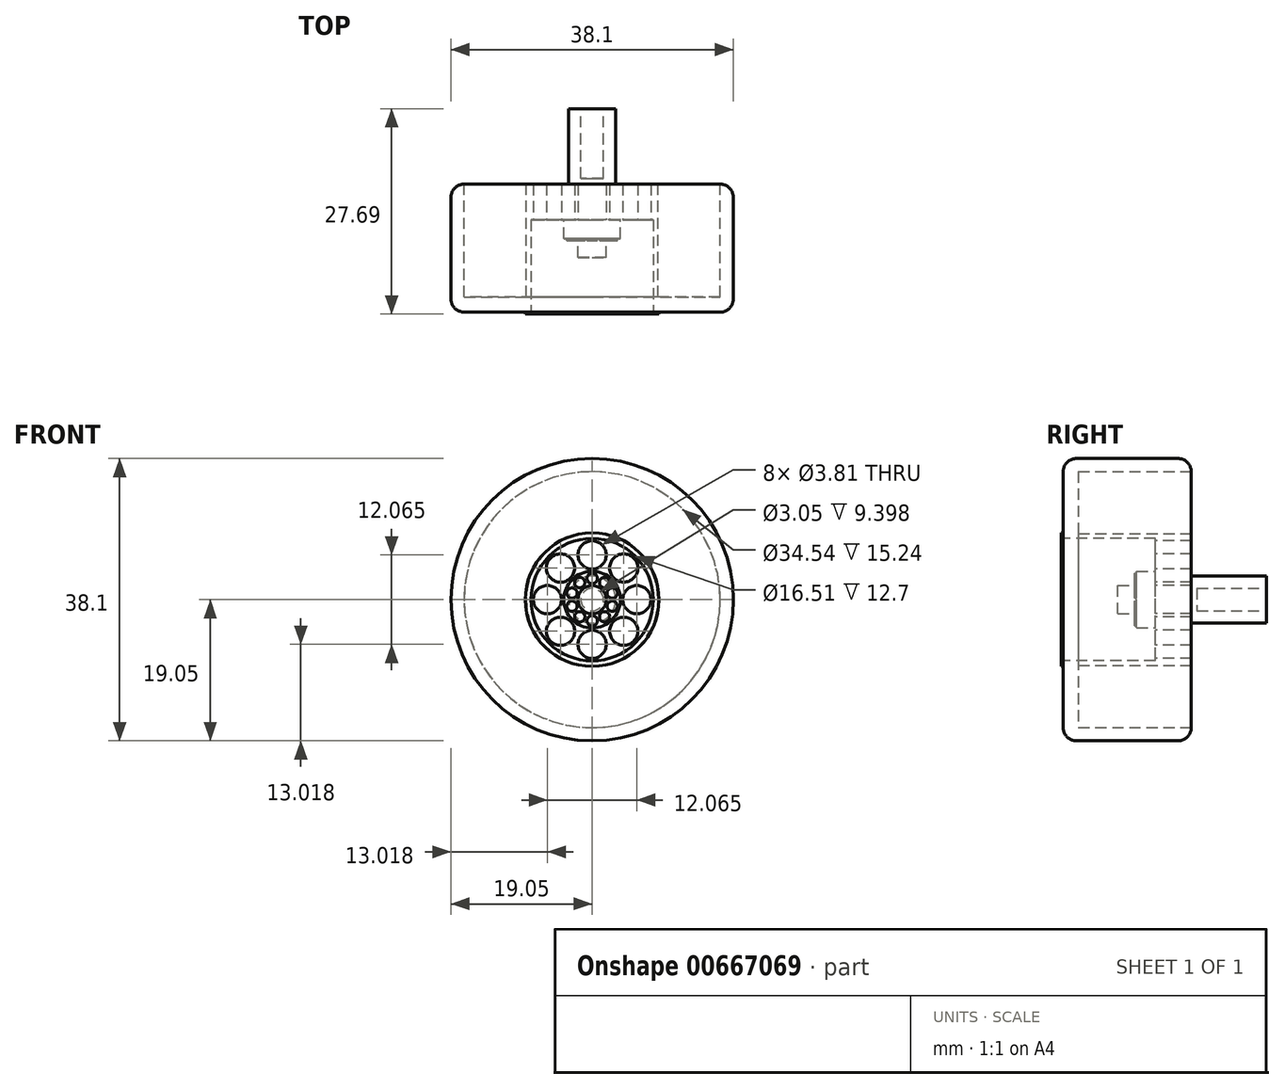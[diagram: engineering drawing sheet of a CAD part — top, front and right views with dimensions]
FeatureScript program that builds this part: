
annotation { "Feature Type Name" : "Feature", "Feature Type Description" : "" }
export const myFeature = defineFeature(function(context is Context, id is Id, definition is map)
    precondition{}
    {
        {
            var Q0;
            Q0=qCreatedBy(makeId("Front.planeOp"),FACE);
            var sketch = newSketch(context, id + "F0", { "sketchPlane" : qUnion([Q0])});
            skCircle(sketch, "E0", {"center": v(0, 0) * mm, "radius": 19.05 * mm});
            skSolve(sketch);
        }
        {
            var Q0;
            Q0=makeQuery(id+"F0.imprint","IMPRINT",FACE,{"disambiguationData":[TD([[makeQuery(id+"F0.imprint","IMPRINT",EDGE,{"derivedFrom":sQuery(id+"F0.wireOp",EDGE,"E0")}),1.0]])]});
            extrude(context, id + "F1", {"entities" : qUnion([Q0]), "depth" : 17.27 * mm, "offsetDistance" : 25.4 * mm});
        }
        {
            var Q0;
            Q0=makeQuery(id+"F1.opExtrude","CAP_FACE",FACE,{"disambiguationData":[OSD([sQuery(id+"F0.wireOp",EDGE,"E0")])],"isStart":true});
            var sketch = newSketch(context, id + "F2", { "sketchPlane" : qUnion([Q0])});
            skCircle(sketch, "E1", {"center": v(0, 0) * mm, "radius": 3.18 * mm});
            skSolve(sketch);
        }
        {
            var Q0;
            Q0=makeQuery(id+"F2.imprint","IMPRINT",FACE,{"disambiguationData":[TD([[makeQuery(id+"F2.imprint","IMPRINT",EDGE,{"derivedFrom":sQuery(id+"F2.wireOp",EDGE,"E1")}),1.0]])]});
            extrude(context, id + "F3", {"entities" : qUnion([Q0]), "operationType" : NewBodyOperationType.ADD, "depth" : 10.16 * mm, "offsetDistance" : 25.4 * mm});
        }
        {
            var Q0;
            Q0=makeQuery(id+"F3.opExtrude","CAP_FACE",FACE,{"disambiguationData":[OSD([sQuery(id+"F2.wireOp",EDGE,"E1")])],"isStart":false});
            var sketch = newSketch(context, id + "F4", { "sketchPlane" : qUnion([Q0])});
            skCircle(sketch, "E2", {"center": v(0, 0) * mm, "radius": 1.52 * mm});
            skSolve(sketch);
        }
        {
            var Q0;
            Q0=makeQuery(id+"F4.imprint","IMPRINT",FACE,{"disambiguationData":[TD([[makeQuery(id+"F4.imprint","IMPRINT",EDGE,{"derivedFrom":sQuery(id+"F4.wireOp",EDGE,"E2")}),1.0]])]});
            extrude(context, id + "F5", {"entities" : qUnion([Q0]), "operationType" : NewBodyOperationType.REMOVE, "oppositeDirection" : true, "depth" : 9.4 * mm, "offsetDistance" : 25.4 * mm});
        }
        {
            var Q0;
            Q0=makeQuery(id+"F1.opExtrude","CAP_FACE",FACE,{"disambiguationData":[OSD([sQuery(id+"F0.wireOp",EDGE,"E0")])],"isStart":true});
            var sketch = newSketch(context, id + "F6", { "sketchPlane" : qUnion([Q0])});
            skCircle(sketch, "E3", {"center": v(0, 0) * mm, "radius": 17.27 * mm});
            skSolve(sketch);
        }
        {
            var Q0;
            Q0=makeQuery(id+"F1.opExtrude","CAP_FACE",FACE,{"disambiguationData":[OSD([sQuery(id+"F0.wireOp",EDGE,"E0")])],"isStart":false});
            var sketch = newSketch(context, id + "F7", { "sketchPlane" : qUnion([Q0])});
            skCircle(sketch, "E4", {"center": v(0, 0) * mm, "radius": 8.9 * mm});
            skCircle(sketch, "E5", {"center": v(0, 0) * mm, "radius": 8.26 * mm});
            skSolve(sketch);
        }
        {
            var Q0;
            Q0=makeQuery(id+"F7.imprint","IMPRINT",FACE,{"disambiguationData":[TD([[makeQuery(id+"F7.imprint","IMPRINT",EDGE,{"derivedFrom":sQuery(id+"F7.wireOp",EDGE,"E5")}),1.0]])]});
            extrude(context, id + "F8", {"entities" : qUnion([Q0]), "operationType" : NewBodyOperationType.REMOVE, "oppositeDirection" : true, "depth" : 12.45 * mm, "offsetDistance" : 25.4 * mm});
        }
        {
            var Q0;
            Q0=makeQuery(id+"F6.imprint","IMPRINT",FACE,{"disambiguationData":[TD([[makeQuery(id+"F6.imprint","IMPRINT",EDGE,{"derivedFrom":sQuery(id+"F6.wireOp",EDGE,"E3")}),1.0]])]});
            var sketch = newSketch(context, id + "F9", { "sketchPlane" : qUnion([Q0])});
            skCircle(sketch, "E6", {"center": v(0, 0) * mm, "radius": 8.9 * mm});
            skSolve(sketch);
        }
        {
            var Q0;
            Q0=makeQuery(id+"F9.imprint","IMPRINT",FACE,{"disambiguationData":[TD([[makeQuery(id+"F9.imprint","IMPRINT",EDGE,{"derivedFrom":sQuery(id+"F9.wireOp",EDGE,"E6")}),-1.0]])]});
            extrude(context, id + "F10", {"entities" : qUnion([Q0]), "operationType" : NewBodyOperationType.REMOVE, "oppositeDirection" : true, "depth" : 15.24 * mm, "offsetDistance" : 25.4 * mm});
        }
        {
            var Q0;
            Q0=makeQuery(id+"F1.opExtrude","CAP_FACE",FACE,{"disambiguationData":[OSD([sQuery(id+"F0.wireOp",EDGE,"E0")])],"isStart":false});
            var sketch = newSketch(context, id + "F11", { "sketchPlane" : qUnion([Q0])});
            skCircle(sketch, "E7", {"center": v(0, 0) * mm, "radius": 9.02 * mm});
            skSolve(sketch);
        }
        {
            var Q0;
            Q0=makeQuery(id+"F11.imprint","IMPRINT",FACE,{"disambiguationData":[TD([[makeQuery(id+"F11.imprint","IMPRINT",EDGE,{"derivedFrom":sQuery(id+"F11.wireOp",EDGE,"E7")}),1.0]])]});
            extrude(context, id + "F12", {"entities" : qUnion([Q0]), "operationType" : NewBodyOperationType.ADD, "depth" : 0.25 * mm, "offsetDistance" : 25.4 * mm});
        }
        {
            var Q0;
            Q0=makeQuery(id+"F8.boolean.opBoolean","COPY",FACE,{"derivedFrom":makeQuery(id+"F8.opExtrude","CAP_FACE",FACE,{"disambiguationData":[OSD([sQuery(id+"F7.wireOp",EDGE,"E5")])],"isStart":false})});
            var sketch = newSketch(context, id + "F13", { "sketchPlane" : qUnion([Q0])});
            skCircle(sketch, "E8", {"center": v(0, 0) * mm, "radius": 1.9 * mm});
            skSolve(sketch);
        }
        {
            var Q0;
            Q0=makeQuery(id+"F13.imprint","IMPRINT",FACE,{"disambiguationData":[TD([[makeQuery(id+"F13.imprint","IMPRINT",EDGE,{"derivedFrom":sQuery(id+"F13.wireOp",EDGE,"E8")}),1.0]])]});
            extrude(context, id + "F14", {"entities" : qUnion([Q0]), "operationType" : NewBodyOperationType.ADD, "depth" : 5.08 * mm, "offsetDistance" : 25.4 * mm});
        }
        {
            var Q0;
            Q0=makeQuery(id+"F8.boolean.opBoolean","COPY",FACE,{"derivedFrom":makeQuery(id+"F8.opExtrude","CAP_FACE",FACE,{"disambiguationData":[OSD([sQuery(id+"F7.wireOp",EDGE,"E5")])],"isStart":false})});
            var sketch = newSketch(context, id + "F15", { "sketchPlane" : qUnion([Q0])});
            skCircle(sketch, "E9", {"center": v(0, 0) * mm, "radius": 3.81 * mm});
            skSolve(sketch);
        }
        {
            var Q0;
            Q0=makeQuery(id+"F15.imprint","IMPRINT",FACE,{"disambiguationData":[TD([[makeQuery(id+"F15.imprint","IMPRINT",EDGE,{"derivedFrom":sQuery(id+"F15.wireOp",EDGE,"E9")}),1.0]])]});
            extrude(context, id + "F16", {"entities" : qUnion([Q0]), "operationType" : NewBodyOperationType.ADD, "depth" : 2.54 * mm, "offsetDistance" : 25.4 * mm});
        }
        {
            var Q0;
            Q0=makeQuery(id+"F8.boolean.opBoolean","COPY",FACE,{"derivedFrom":makeQuery(id+"F8.opExtrude","CAP_FACE",FACE,{"disambiguationData":[OSD([sQuery(id+"F7.wireOp",EDGE,"E5")])],"isStart":false})});
            var sketch = newSketch(context, id + "F17", { "sketchPlane" : qUnion([Q0])});
            skCircle(sketch, "E10", {"center": v(0, 6.03) * mm, "radius": 1.9 * mm});
            skCircle(sketch, "E11", {"center": v(0, -6.03) * mm, "radius": 1.9 * mm});
            skCircle(sketch, "E12", {"center": v(4.27, -4.26) * mm, "radius": 1.9 * mm});
            skCircle(sketch, "E13", {"center": v(6.03, 0) * mm, "radius": 1.9 * mm});
            skCircle(sketch, "E14", {"center": v(4.26, 4.27) * mm, "radius": 1.9 * mm});
            skCircle(sketch, "E15", {"center": v(-4.27, 4.26) * mm, "radius": 1.9 * mm});
            skCircle(sketch, "E16", {"center": v(-6.03, 0) * mm, "radius": 1.9 * mm});
            skCircle(sketch, "E17", {"center": v(-4.26, -4.27) * mm, "radius": 1.9 * mm});
            skSolve(sketch);
        }
        {
            var Q0;
            Q0=makeQuery(id+"F17.imprint","IMPRINT",FACE,{"disambiguationData":[TD([[makeQuery(id+"F17.imprint","IMPRINT",EDGE,{"derivedFrom":sQuery(id+"F17.wireOp",EDGE,"E15")}),1.0]])]});
            var Q1;
            Q1=makeQuery(id+"F17.imprint","IMPRINT",FACE,{"disambiguationData":[TD([[makeQuery(id+"F17.imprint","IMPRINT",EDGE,{"derivedFrom":sQuery(id+"F17.wireOp",EDGE,"E10")}),1.0]])]});
            var Q2;
            Q2=makeQuery(id+"F17.imprint","IMPRINT",FACE,{"disambiguationData":[TD([[makeQuery(id+"F17.imprint","IMPRINT",EDGE,{"derivedFrom":sQuery(id+"F17.wireOp",EDGE,"E14")}),1.0]])]});
            var Q3;
            Q3=makeQuery(id+"F17.imprint","IMPRINT",FACE,{"disambiguationData":[TD([[makeQuery(id+"F17.imprint","IMPRINT",EDGE,{"derivedFrom":sQuery(id+"F17.wireOp",EDGE,"E13")}),1.0]])]});
            var Q4;
            Q4=makeQuery(id+"F17.imprint","IMPRINT",FACE,{"disambiguationData":[TD([[makeQuery(id+"F17.imprint","IMPRINT",EDGE,{"derivedFrom":sQuery(id+"F17.wireOp",EDGE,"E12")}),1.0]])]});
            var Q5;
            Q5=makeQuery(id+"F17.imprint","IMPRINT",FACE,{"disambiguationData":[TD([[makeQuery(id+"F17.imprint","IMPRINT",EDGE,{"derivedFrom":sQuery(id+"F17.wireOp",EDGE,"E11")}),1.0]])]});
            var Q6;
            Q6=makeQuery(id+"F17.imprint","IMPRINT",FACE,{"disambiguationData":[TD([[makeQuery(id+"F17.imprint","IMPRINT",EDGE,{"derivedFrom":sQuery(id+"F17.wireOp",EDGE,"E17")}),1.0]])]});
            var Q7;
            Q7=makeQuery(id+"F17.imprint","IMPRINT",FACE,{"disambiguationData":[TD([[makeQuery(id+"F17.imprint","IMPRINT",EDGE,{"derivedFrom":sQuery(id+"F17.wireOp",EDGE,"E16")}),1.0]])]});
            extrude(context, id + "F18", {"entities" : qUnion([Q0, Q1, Q2, Q3, Q4, Q5, Q6, Q7]), "operationType" : NewBodyOperationType.REMOVE, "endBound" : BoundingType.THROUGH_ALL, "oppositeDirection" : true, "depth" : 25.4 * mm, "offsetDistance" : 25.4 * mm});
        }
        {
            var Q0;
            Q0=makeQuery(id+"F16.opExtrude","CAP_FACE",FACE,{"disambiguationData":[OSD([sQuery(id+"F13.wireOp",EDGE,"E8"),sQuery(id+"F15.wireOp",EDGE,"E9")])],"isStart":false});
            var sketch = newSketch(context, id + "F19", { "sketchPlane" : qUnion([Q0])});
            skCircle(sketch, "E18", {"center": v(0, 2.86) * mm, "radius": 0.7 * mm});
            skCircle(sketch, "E19.1.0", {"center": v(-1.68, 2.31) * mm, "radius": 0.7 * mm});
            skCircle(sketch, "E19.2.0", {"center": v(-2.72, 0.88) * mm, "radius": 0.7 * mm});
            skCircle(sketch, "E19.3.0", {"center": v(-2.72, -0.88) * mm, "radius": 0.7 * mm});
            skCircle(sketch, "E19.4.0", {"center": v(-1.68, -2.31) * mm, "radius": 0.7 * mm});
            skCircle(sketch, "E19.5.0", {"center": v(0, -2.86) * mm, "radius": 0.7 * mm});
            skCircle(sketch, "E19.6.0", {"center": v(1.68, -2.31) * mm, "radius": 0.7 * mm});
            skCircle(sketch, "E19.7.0", {"center": v(2.72, -0.88) * mm, "radius": 0.7 * mm});
            skCircle(sketch, "E19.8.0", {"center": v(2.72, 0.88) * mm, "radius": 0.7 * mm});
            skCircle(sketch, "E19.9.0", {"center": v(1.68, 2.31) * mm, "radius": 0.7 * mm});
            skPoint(sketch, "E19.center", {"position": v(0, 0) * mm});
            skSolve(sketch);
        }
        {
            var Q0;
            Q0=makeQuery(id+"F19.imprint","IMPRINT",FACE,{"disambiguationData":[TD([[makeQuery(id+"F19.imprint","IMPRINT",EDGE,{"derivedFrom":sQuery(id+"F19.wireOp",EDGE,"E19.1.0")}),1.0]])]});
            var Q1;
            Q1=makeQuery(id+"F19.imprint","IMPRINT",FACE,{"disambiguationData":[TD([[makeQuery(id+"F19.imprint","IMPRINT",EDGE,{"derivedFrom":sQuery(id+"F19.wireOp",EDGE,"E18")}),1.0]])]});
            var Q2;
            Q2=makeQuery(id+"F19.imprint","IMPRINT",FACE,{"disambiguationData":[TD([[makeQuery(id+"F19.imprint","IMPRINT",EDGE,{"derivedFrom":sQuery(id+"F19.wireOp",EDGE,"E19.9.0")}),1.0]])]});
            var Q3;
            Q3=makeQuery(id+"F19.imprint","IMPRINT",FACE,{"disambiguationData":[TD([[makeQuery(id+"F19.imprint","IMPRINT",EDGE,{"derivedFrom":sQuery(id+"F19.wireOp",EDGE,"E19.8.0")}),1.0]])]});
            var Q4;
            Q4=makeQuery(id+"F19.imprint","IMPRINT",FACE,{"disambiguationData":[TD([[makeQuery(id+"F19.imprint","IMPRINT",EDGE,{"derivedFrom":sQuery(id+"F19.wireOp",EDGE,"E19.6.0")}),1.0]])]});
            var Q5;
            Q5=makeQuery(id+"F19.imprint","IMPRINT",FACE,{"disambiguationData":[TD([[makeQuery(id+"F19.imprint","IMPRINT",EDGE,{"derivedFrom":sQuery(id+"F19.wireOp",EDGE,"E19.5.0")}),1.0]])]});
            var Q6;
            Q6=makeQuery(id+"F19.imprint","IMPRINT",FACE,{"disambiguationData":[TD([[makeQuery(id+"F19.imprint","IMPRINT",EDGE,{"derivedFrom":sQuery(id+"F19.wireOp",EDGE,"E19.7.0")}),1.0]])]});
            var Q7;
            Q7=makeQuery(id+"F19.imprint","IMPRINT",FACE,{"disambiguationData":[TD([[makeQuery(id+"F19.imprint","IMPRINT",EDGE,{"derivedFrom":sQuery(id+"F19.wireOp",EDGE,"E19.4.0")}),1.0]])]});
            var Q8;
            Q8=makeQuery(id+"F19.imprint","IMPRINT",FACE,{"disambiguationData":[TD([[makeQuery(id+"F19.imprint","IMPRINT",EDGE,{"derivedFrom":sQuery(id+"F19.wireOp",EDGE,"E19.3.0")}),1.0]])]});
            var Q9;
            Q9=makeQuery(id+"F19.imprint","IMPRINT",FACE,{"disambiguationData":[TD([[makeQuery(id+"F19.imprint","IMPRINT",EDGE,{"derivedFrom":sQuery(id+"F19.wireOp",EDGE,"E19.2.0")}),1.0]])]});
            extrude(context, id + "F20", {"entities" : qUnion([Q0, Q1, Q2, Q3, Q4, Q5, Q6, Q7, Q8, Q9]), "operationType" : NewBodyOperationType.ADD, "depth" : 0.25 * mm, "offsetDistance" : 25.4 * mm});
        }
        {
            var Q0;
            Q0=makeQuery(id+"F1.opExtrude","CAP_EDGE",EDGE,{"disambiguationData":[OSD([sQuery(id+"F0.wireOp",EDGE,"E0")])],"isStart":false});
            fillet(context, id + "F21", {"entities" : qUnion([Q0]), "radius" : 1.78 * mm, "tangentPropagation" : true, "allowEdgeOverflow" : false});
        }
        {
            var Q0;
            Q0=makeQuery(id+"F1.opExtrude","CAP_EDGE",EDGE,{"disambiguationData":[OSD([sQuery(id+"F0.wireOp",EDGE,"E0")])],"isStart":true});
            fillet(context, id + "F22", {"entities" : qUnion([Q0]), "radius" : 1.78 * mm, "tangentPropagation" : true, "allowEdgeOverflow" : false});
        }
    });
